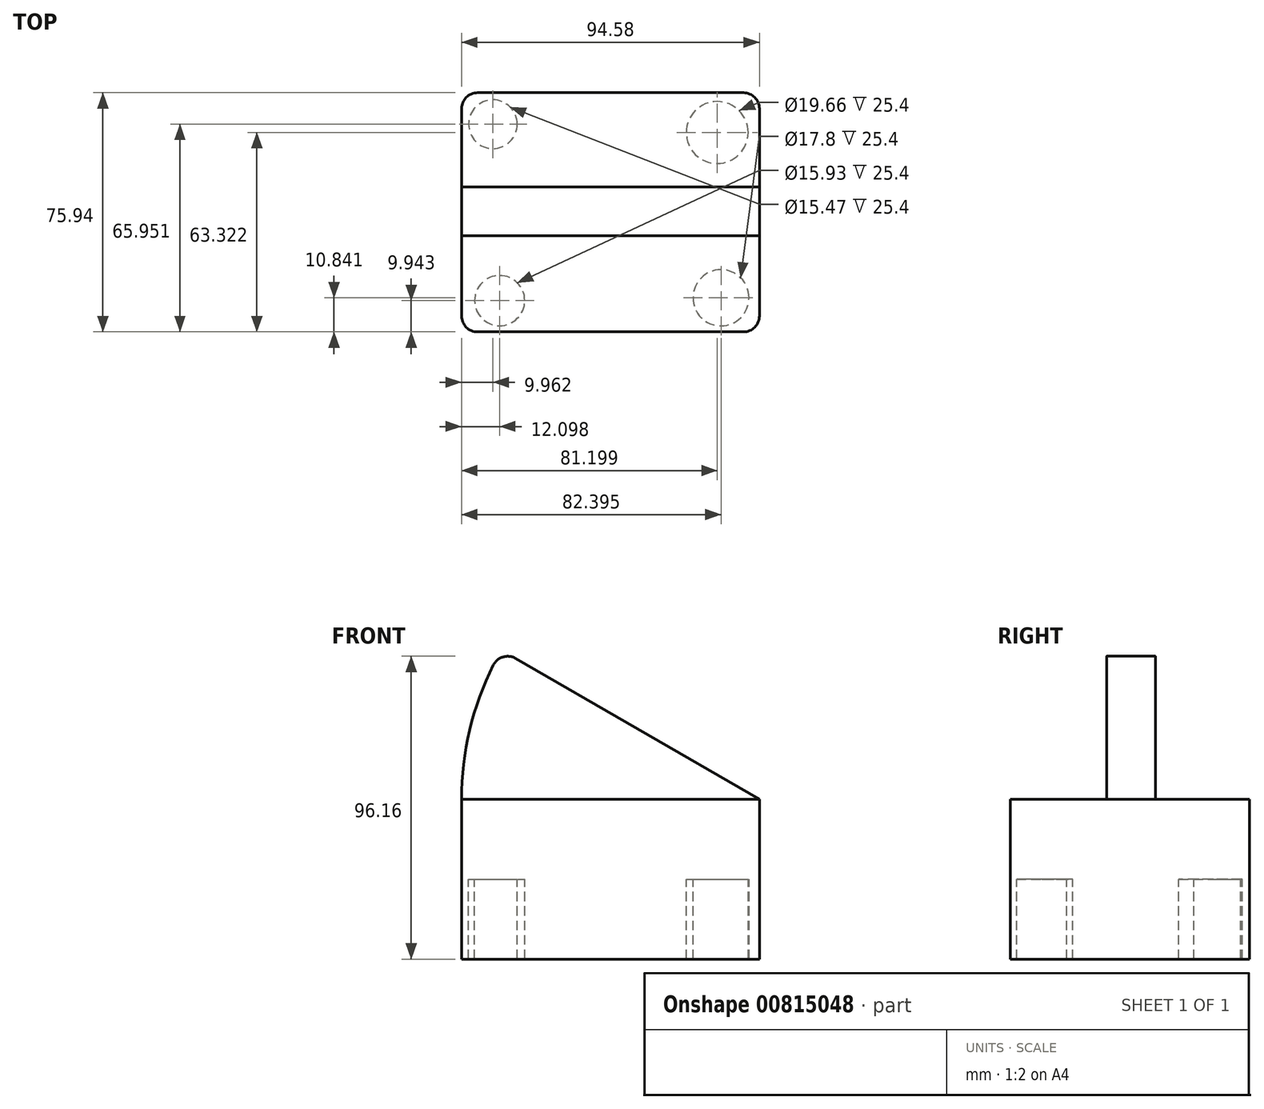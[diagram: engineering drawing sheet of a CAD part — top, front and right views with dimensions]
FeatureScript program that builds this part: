
annotation { "Feature Type Name" : "Feature", "Feature Type Description" : "" }
export const myFeature = defineFeature(function(context is Context, id is Id, definition is map)
    precondition{}
    {
        {
            var Q0;
            Q0=qCreatedBy(makeId("Top.planeOp"),FACE);
            var sketch = newSketch(context, id + "F0", { "sketchPlane" : qUnion([Q0])});
            skLineSegment(sketch, "E0.bottom", {"start": v(47.3, -37.97) * mm, "end": v(-47.3, -37.97) * mm});
            skLineSegment(sketch, "E0.top", {"start": v(47.3, 37.97) * mm, "end": v(-47.3, 37.97) * mm});
            skLineSegment(sketch, "E0.left", {"start": v(47.3, -37.97) * mm, "end": v(47.3, 37.97) * mm});
            skLineSegment(sketch, "E0.right", {"start": v(-47.3, -37.97) * mm, "end": v(-47.3, 37.97) * mm});
            skPoint(sketch, "E0.middle", {"position": v(0, 0) * mm});
            skLineSegment(sketch, "E1.bottom", {"start": v(-47.3, 14.68) * mm, "end": v(47.3, 14.68) * mm});
            skLineSegment(sketch, "E1.top", {"start": v(-47.3, -13.75) * mm, "end": v(47.3, -13.75) * mm});
            skLineSegment(sketch, "E1.left", {"start": v(-47.3, 14.68) * mm, "end": v(-47.3, -13.75) * mm});
            skLineSegment(sketch, "E1.right", {"start": v(47.3, 14.68) * mm, "end": v(47.3, -13.75) * mm});
            skSolve(sketch);
        }
        {
            var Q0;
            Q0=makeQuery(id+"F0.imprint","IMPRINT",FACE,{"disambiguationData":[TD([[makeQuery(id+"F0.imprint","IMPRINT",EDGE,{"derivedFrom":sQuery(id+"F0.wireOp",EDGE,"E1.bottom")}),-1.0]])]});
            var Q1;
            {var subQ0=sQuery(id+"F0.wireOp",EDGE,"E0.bottom");Q1=makeQuery(id+"F0.imprint","IMPRINT",FACE,{"disambiguationData":[TD([[makeQuery(id+"F0.imprint","IMPRINT",EDGE,{"derivedFrom":subQ0}),-1.0]])]});}
            var Q2;
            {var subQ0=sQuery(id+"F0.wireOp",EDGE,"E0.top");Q2=makeQuery(id+"F0.imprint","IMPRINT",FACE,{"disambiguationData":[TD([[makeQuery(id+"F0.imprint","IMPRINT",EDGE,{"derivedFrom":subQ0}),1.0]])]});}
            extrude(context, id + "F1", {"entities" : qUnion([Q0, Q1, Q2]), "depth" : 25.4 * mm, "offsetDistance" : 25.4 * mm});
        }
        {
            var Q0;
            Q0=makeQuery(id+"F1.opExtrude","CAP_FACE",FACE,{"disambiguationData":[OSD([sQuery(id+"F0.wireOp",EDGE,"E0.bottom"),sQuery(id+"F0.wireOp",EDGE,"E0.top"),sQuery(id+"F0.wireOp",EDGE,"E0.left"),sQuery(id+"F0.wireOp",EDGE,"E0.right"),sQuery(id+"F0.wireOp",EDGE,"E1.left"),sQuery(id+"F0.wireOp",EDGE,"E1.right")])],"isStart":false});
            var sketch = newSketch(context, id + "F2", { "sketchPlane" : qUnion([Q0])});
            skLineSegment(sketch, "E2.bottom", {"start": v(-47.3, 8.1) * mm, "end": v(47.3, 8.1) * mm});
            skLineSegment(sketch, "E2.top", {"start": v(-47.3, -7.44) * mm, "end": v(47.3, -7.44) * mm});
            skLineSegment(sketch, "E2.left", {"start": v(-47.3, 8.1) * mm, "end": v(-47.3, -7.44) * mm});
            skLineSegment(sketch, "E2.right", {"start": v(47.3, 8.1) * mm, "end": v(47.3, -7.44) * mm});
            skSolve(sketch);
        }
        {
            var Q0;
            Q0=makeQuery(id+"F2.imprint","IMPRINT",FACE,{"disambiguationData":[TD([[makeQuery(id+"F2.imprint","IMPRINT",EDGE,{"derivedFrom":sQuery(id+"F2.wireOp",EDGE,"E2.bottom")}),-1.0]])]});
            var Q1;
            Q1=sQuery(id+"F2.wireOp",EDGE,"E2.right");
            revolve(context, id + "F3", {"operationType" : NewBodyOperationType.ADD, "surfaceOperationType" : NewSurfaceOperationType.NEW, "entities" : qUnion([Q0]), "axis" : qUnion([Q1]), "revolveType" : RevolveType.ONE_DIRECTION, "oppositeDirection" : true, "angle" : 30 * degree});
        }
        {
            var Q0;
            Q0=makeQuery(id+"F1.opExtrude","SWEPT_EDGE",EDGE,{"disambiguationData":[OSD([sQuery(id+"F0.wireOp",EDGE,"E0.bottom"),sQuery(id+"F0.wireOp",EDGE,"E0.right")])]});
            var Q1;
            Q1=makeQuery(id+"F1.opExtrude","SWEPT_EDGE",EDGE,{"disambiguationData":[OSD([sQuery(id+"F0.wireOp",EDGE,"E0.bottom"),sQuery(id+"F0.wireOp",EDGE,"E0.left")])]});
            fillet(context, id + "F4", {"entities" : qUnion([Q0, Q1]), "radius" : 5.08 * mm, "tangentPropagation" : true, "allowEdgeOverflow" : false});
        }
        {
            var Q0;
            Q0=makeQuery(id+"F1.opExtrude","SWEPT_EDGE",EDGE,{"disambiguationData":[OSD([sQuery(id+"F0.wireOp",EDGE,"E0.top"),sQuery(id+"F0.wireOp",EDGE,"E0.left")])]});
            fillet(context, id + "F5", {"entities" : qUnion([Q0]), "radius" : 5.08 * mm, "tangentPropagation" : true, "allowEdgeOverflow" : false});
        }
        {
            var Q0;
            Q0=makeQuery(id+"F1.opExtrude","SWEPT_EDGE",EDGE,{"disambiguationData":[OSD([sQuery(id+"F0.wireOp",EDGE,"E0.top"),sQuery(id+"F0.wireOp",EDGE,"E0.right")])]});
            var Q1;
            Q1=makeQuery(id+"F3.opRevolve","CAP_EDGE",EDGE,{"disambiguationData":[OSD([sQuery(id+"F2.wireOp",EDGE,"E2.left")])],"isStart":false});
            fillet(context, id + "F6", {"entities" : qUnion([Q0, Q1]), "radius" : 5.08 * mm, "tangentPropagation" : true, "allowEdgeOverflow" : false});
        }
        {
            var Q0;
            Q0=makeQuery(id+"F1.opExtrude","CAP_FACE",FACE,{"disambiguationData":[OSD([sQuery(id+"F0.wireOp",EDGE,"E0.bottom"),sQuery(id+"F0.wireOp",EDGE,"E0.top"),sQuery(id+"F0.wireOp",EDGE,"E0.left"),sQuery(id+"F0.wireOp",EDGE,"E0.right"),sQuery(id+"F0.wireOp",EDGE,"E1.left"),sQuery(id+"F0.wireOp",EDGE,"E1.right")])],"isStart":true});
            var sketch = newSketch(context, id + "F7", { "sketchPlane" : qUnion([Q0])});
            skCircle(sketch, "E3", {"center": v(-37.33, -27.98) * mm, "radius": 7.74 * mm});
            skCircle(sketch, "E4", {"center": v(-35.2, 28.03) * mm, "radius": 7.97 * mm});
            skCircle(sketch, "E5", {"center": v(35.1, 27.13) * mm, "radius": 8.9 * mm});
            skCircle(sketch, "E6", {"center": v(33.9, -25.35) * mm, "radius": 9.83 * mm});
            skSolve(sketch);
        }
        {
            var Q0;
            Q0=makeQuery(id+"F7.imprint","IMPRINT",FACE,{"disambiguationData":[TD([[makeQuery(id+"F7.imprint","IMPRINT",EDGE,{"derivedFrom":sQuery(id+"F7.wireOp",EDGE,"E3")}),-1.0]])]});
            extrude(context, id + "F8", {"entities" : qUnion([Q0]), "operationType" : NewBodyOperationType.ADD, "depth" : 25.4 * mm, "offsetDistance" : 25.4 * mm});
        }
    });
